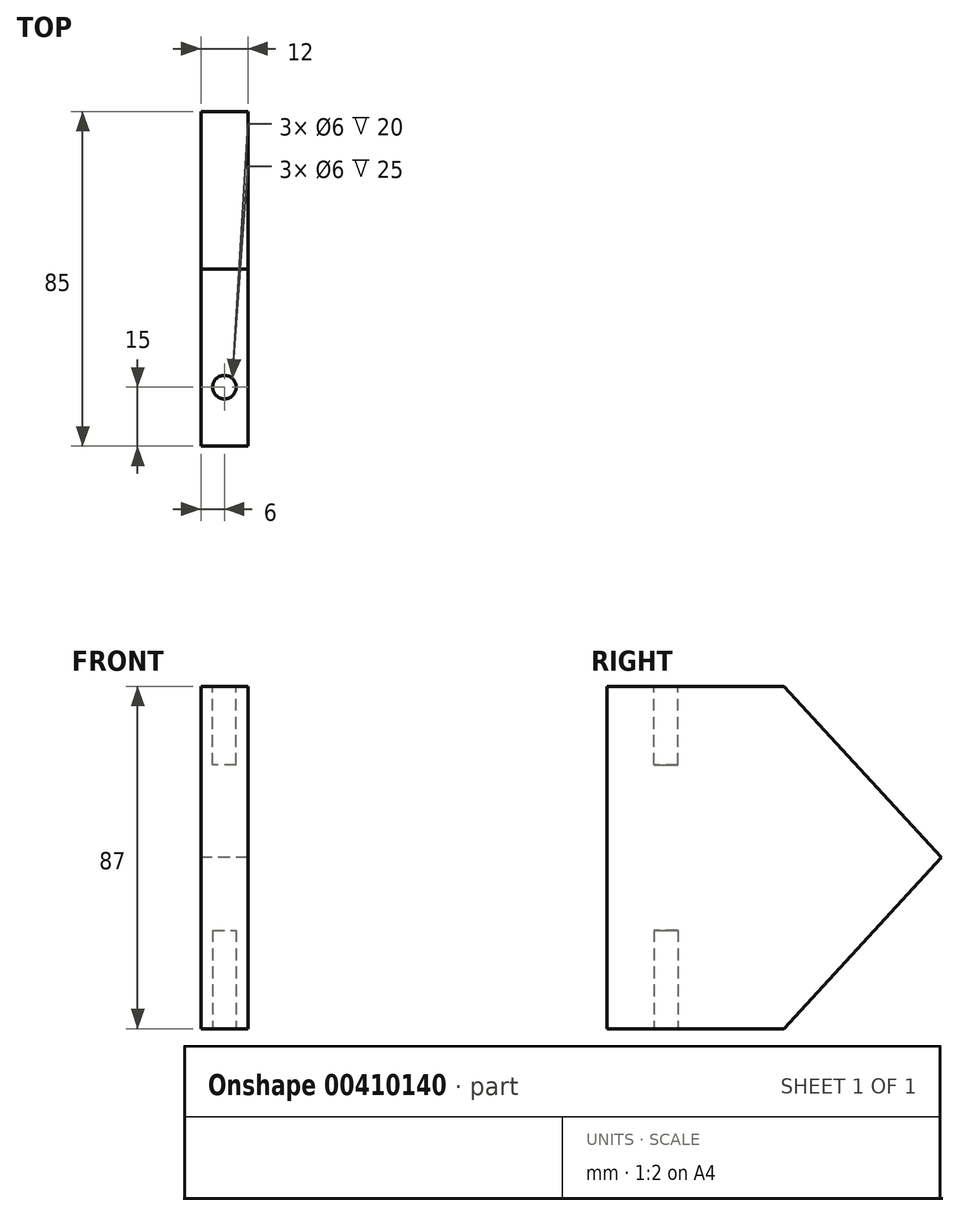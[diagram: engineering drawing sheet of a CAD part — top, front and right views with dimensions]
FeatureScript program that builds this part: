
annotation { "Feature Type Name" : "Feature", "Feature Type Description" : "" }
export const myFeature = defineFeature(function(context is Context, id is Id, definition is map)
    precondition{}
    {
        {
            var Q0;
            Q0=qCreatedBy(makeId("Right.planeOp"),FACE);
            var sketch = newSketch(context, id + "F0", { "sketchPlane" : qUnion([Q0])});
            skLineSegment(sketch, "E0.bottom", {"start": v(0, 0) * mm, "end": v(105, 0) * mm});
            skLineSegment(sketch, "E0.top", {"start": v(0, 87) * mm, "end": v(105, 87) * mm});
            skLineSegment(sketch, "E0.left", {"start": v(0, 0) * mm, "end": v(0, 87) * mm});
            skLineSegment(sketch, "E0.right", {"start": v(105, 0) * mm, "end": v(105, 87) * mm, "construction": true});
            skLineSegment(sketch, "E1", {"start": v(-42.15, 43.5) * mm, "end": v(145, 43.5) * mm, "construction": true});
            skPoint(sketch, "E2", {"position": v(0, 43.5) * mm});
            skPoint(sketch, "E3", {"position": v(105, 43.5) * mm});
            skLineSegment(sketch, "E4", {"start": v(105, 0) * mm, "end": v(145, 43.5) * mm});
            skLineSegment(sketch, "E5", {"start": v(145, 43.5) * mm, "end": v(105, 87) * mm});
            skSolve(sketch);
        }
        {
            var Q0;
            Q0=qSketchRegion(id+"F0",true);
            extrude(context, id + "F1", {"entities" : qUnion([Q0]), "depth" : 12 * mm});
        }
        {
            var Q0;
            Q0=makeQuery(id+"F1.opExtrude","SWEPT_FACE",FACE,{"disambiguationData":[OSD([sQuery(id+"F0.wireOp",EDGE,"E0.top")])]});
            var sketch = newSketch(context, id + "F2", { "sketchPlane" : qUnion([Q0])});
            skCircle(sketch, "E6", {"center": v(6, 15) * mm, "radius": 3 * mm});
            skLineSegment(sketch, "E7", {"start": v(6, 0) * mm, "end": v(6, 15) * mm, "construction": true});
            skCircle(sketch, "E8.0.1.0", {"center": v(6, 45) * mm, "radius": 3 * mm});
            skCircle(sketch, "E8.0.2.0", {"center": v(6, 75) * mm, "radius": 3 * mm});
            skLineSegment(sketch, "E8.direction1", {"start": v(6, 15) * mm, "end": v(31, 15) * mm, "construction": true});
            skLineSegment(sketch, "E8.direction2", {"start": v(6, 15) * mm, "end": v(6, 45) * mm, "construction": true});
            skSolve(sketch);
        }
        {
            var Q0;
            Q0 = qSketchRegion(id + "F2", true);
            extrude(context, id + "F3", {"entities" : qUnion([Q0]), "operationType" : NewBodyOperationType.REMOVE, "oppositeDirection" : true, "depth" : 20 * mm});
        }
        {
            var Q0;
            Q0=makeQuery(id+"F1.opExtrude","SWEPT_FACE",FACE,{"disambiguationData":[OSD([sQuery(id+"F0.wireOp",EDGE,"E0.bottom")])]});
            var sketch = newSketch(context, id + "F4", { "sketchPlane" : qUnion([Q0])});
            skCircle(sketch, "E9.0", {"center": v(6, -15) * mm, "radius": 3 * mm});
            skLineSegment(sketch, "E9.1", {"start": v(6, 0) * mm, "end": v(6, -15) * mm});
            skCircle(sketch, "E9.2", {"center": v(6, -45) * mm, "radius": 3 * mm});
            skCircle(sketch, "E9.3", {"center": v(6, -75) * mm, "radius": 3 * mm});
            skLineSegment(sketch, "E9.4", {"start": v(6, -15) * mm, "end": v(31, -15) * mm});
            skLineSegment(sketch, "E9.5", {"start": v(6, -15) * mm, "end": v(6, -45) * mm});
            skSolve(sketch);
        }
        {
            var Q0;
            Q0 = qSketchRegion(id + "F4", true);
            extrude(context, id + "F5", {"entities" : qUnion([Q0]), "operationType" : NewBodyOperationType.REMOVE, "oppositeDirection" : true, "depth" : 25 * mm});
        }
        {
            var Q0;
            Q0=makeQuery(id+"F1.opExtrude","CAP_FACE",FACE,{"disambiguationData":[OSD([sQuery(id+"F0.wireOp",EDGE,"E0.bottom"),sQuery(id+"F0.wireOp",EDGE,"E0.top"),sQuery(id+"F0.wireOp",EDGE,"E0.left"),sQuery(id+"F0.wireOp",EDGE,"E4"),sQuery(id+"F0.wireOp",EDGE,"E5")])],"isStart":true});
            var sketch = newSketch(context, id + "F6", { "sketchPlane" : qUnion([Q0])});
            skLineSegment(sketch, "E10", {"start": v(-6, 0) * mm, "end": v(-6, 87) * mm, "construction": true});
            skCircle(sketch, "E11", {"center": v(-6, 77) * mm, "radius": 2 * mm});
            skCircle(sketch, "E12", {"center": v(-6, 10) * mm, "radius": 2 * mm});
            skSolve(sketch);
        }
        {
            var Q0;
            Q0 = qSketchRegion(id + "F6", true);
            extrude(context, id + "F7", {"entities" : qUnion([Q0]), "operationType" : NewBodyOperationType.REMOVE, "oppositeDirection" : true, "depth" : 25 * mm});
        }
        {
            var Q0;
            Q0=makeQuery(id+"F1.opExtrude","CAP_FACE",FACE,{"disambiguationData":[OSD([sQuery(id+"F0.wireOp",EDGE,"E0.bottom"),sQuery(id+"F0.wireOp",EDGE,"E0.top"),sQuery(id+"F0.wireOp",EDGE,"E0.left"),sQuery(id+"F0.wireOp",EDGE,"E4"),sQuery(id+"F0.wireOp",EDGE,"E5")])],"isStart":false});
            var sketch = newSketch(context, id + "F8", { "sketchPlane" : qUnion([Q0])});
            skLineSegment(sketch, "E13.bottom", {"start": v(0, 0) * mm, "end": v(60, 0) * mm});
            skLineSegment(sketch, "E13.top", {"start": v(0, 87) * mm, "end": v(60, 87) * mm});
            skLineSegment(sketch, "E13.left", {"start": v(0, 0) * mm, "end": v(0, 87) * mm});
            skLineSegment(sketch, "E13.right", {"start": v(60, 0) * mm, "end": v(60, 87) * mm});
            skSolve(sketch);
        }
        {
            var Q0;
            Q0 = qSketchRegion(id + "F8", true);
            extrude(context, id + "F9", {"entities" : qUnion([Q0]), "operationType" : NewBodyOperationType.REMOVE, "oppositeDirection" : true, "depth" : 25 * mm, "offsetDistance" : 25 * mm});
        }
    });
